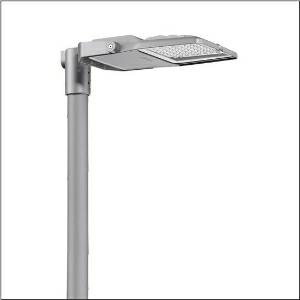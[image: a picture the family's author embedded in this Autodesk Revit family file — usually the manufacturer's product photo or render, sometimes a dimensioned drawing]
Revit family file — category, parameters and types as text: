
# Revit family: floodlight_fl_21_mini___pl43_5xa7776c2a3a_c8bd
name_source: partatom
category: Lighting Fixtures
units: mm (PartAtom-declared; Revit-internal decimal feet)

## family parameters
Cut with Voids When Loaded = No
Host = Face
Light Source = No
Part Type = Normal
Room Calculation Point = No
Round Connector Dimension = Use Diameter
Shared = No

## types (1)
- --- (1 x LED, 12500 lm, 89 W, 3000K)
    Apparent Load = 89 VA
    CIE Flux Codes = 27 78 99 100 100
    Color Rendering = 70
    Color Temperature = 3000K
    Default Elevation = 1800 mm
    Description = Floodlight FL 21 mini, floodlight, primary light control with lens, of PMMA, primary optical cover: protective disc, of toughened safety glass, transparent, light distribution: PL43, light emission: direct distribution, installation type: surface-mounted, LED, High Power LED, rated luminous flux: 12.500lm, luminous efficacy: 140lm/W, light colour: 730, colour temperature: 3000K, control gear: Smart Interface (Zhaga), control: flexible luminous flux parameterisation, time-dependent luminous flux control, constant luminous flux control, overheat protection, pre-setting: logarithmic dimming characteristic, with terminal, 6-pole, mains connection: 220..240V, AC, 50/60Hz, start of lifetime: 89W, end of service life: 94W, reduction: 43W, luminaire housing, of diecast aluminium, powder-coated, SITECO metallic grey (DB 702S), corrosivity category C5 mid according to DIN EN ISO 12944, suitable for swimming pools, chlorine-resistant, sealing non-destructively replaceable, please order mast flange separately, mast bracket, of steel, galvanised, powder-coated, SITECO metallic grey (DB 702S), Smart Interface below and above, protection rating (complete): IP66, insulation class (complete): insulation class II (safety insulation), certification: CE, ENEC, VDE, protection symbol: D, impact resistance: IK08, permissible operating ambient temperature: -40..+40°C, permissible operating ambient temperature for outdoor applications: -40..+50°C, standard: DIN EN 12944, LABS conformity tested according to VDMA 24364:2018-05, packaging unit: 1 piece

Light Distribution: PL43
    Height = 70 mm
    Lamp = 1 x LED
    Lamp Light Flux = 12500 lm
    Lamp Power = 89 W
    Lamp count = 1
    Length = 485 mm
    Luminous efficacy = 140 lm/W
    Manufacturer = Siteco
    ModVariant = No
    Model = 5XA7776C2A3A
    Number of Poles = 1
    OnlyDefault = Yes
    Power Factor = 1
    Product Name = Floodlight FL 21 mini | PL43
    Product group = floodlight | pylon annexe
    ProductGroupID = 6201
    Protection Class = Protection class II
    Protection Degree = IP 66
    RLX_Detail_Level = 1
    RLX_Emergency_Light_Flux = 0 lm
    RLX_Emergency_Type = 0
    RLX_Emergency_Type_DB = No
    RlxData = <blob elided: 101005 chars, md5=a922d2c4>
    Socket = socket
    Standby Power = 0 W
    System Light Flux = 12500 lm
    System Power = 89 W
    Type Comments = factory setting: luminous flux: 100 % | dim-lin: 254 | 456 mA
    Type Image = l_1007125.jpg
    URL = http://relux.com
    VarID = @adj_160549
    Voltage = 0 V
    Weight = 0.00 kg
    Width = 337 mm

## geometry (parser evidence)
native form markers: Blend x4, Sweep x11
no freeform markers — native parametric forms only
